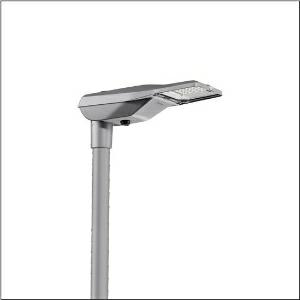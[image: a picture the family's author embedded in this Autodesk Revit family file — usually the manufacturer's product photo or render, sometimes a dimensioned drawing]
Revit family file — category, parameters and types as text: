
# Revit family: streetlight_sl_21_iq_micro___st1_0ab_5xe1m31u08db_013b
name_source: partatom
category: Lighting Fixtures
units: mm (PartAtom-declared; Revit-internal decimal feet)

## family parameters
Cut with Voids When Loaded = No
Host = Face
Light Source = No
Part Type = Normal
Room Calculation Point = No
Round Connector Dimension = Use Diameter
Shared = No

## types (1)
- --- (1 x LED, 4490 lm, 39.1 W, 3000K)
    Apparent Load = 39 VA
    CIE Flux Codes = 38 73 97 100 100
    Color Rendering = 70
    Color Temperature = 3000K
    Default Elevation = 1800 mm
    Description = Streetlight SL 21 iQ micro, mast luminaire, primary light control with lens, of PMMA, primary optical cover: cover, of toughened safety glass, transparent, light distribution: ST1.0aB, light emission: direct distribution, primary light characteristic: asymmetric, installation type: post-top, side-entry, LED, High Power LED, rated luminous flux: 4.490lm, luminous efficacy: 115lm/W, light colour: 730, colour temperature: 3000K, control gear: iQ-Street Remote, D4i with power reduction, control: pre-setting: logarithmic dimming characteristic, Street-Remote, Auto-Match, Temp-Guard, Lumen-Switch, Night-Set, Smart-Wire, Light-Fading, Desk-Remote (wireless, voltage-free reading and setting of iQ features in the workshop via application-optimized NFC function/RFID function), optimised constant luminous flux control (CLO 2.0), mains connection: 220..240V, AC, 50/60Hz, start of lifetime: 39W, end of service life: 41W, reduction: 17W, luminaire housing, of diecast aluminium, powder-coated, SITECO metallic grey (DB 702S), corrosivity category C5 high according to DIN EN ISO 12944, please order mast flange separately, inclination adjustable: 0°, 5°, 10°, 15°, sealing non-destructively replaceable, multi-level sealing system, length: 528mm, width: 235mm, height: 110mm, mast flange for spigot size: 42mm (side-entry): 5XC10008XM4, 60/48mm (side-entry/post-top): 5XC10108XM2, 76/60mm (side-entry/post-top): 5XC10108XM1, mounting height: 4..8m, Smart Interface below, protection rating (complete): IP66, insulation class (complete): insulation class II (safety insulation), certification: CE, ENEC, ENEC+, VDE, impact resistance: IK10, permissible operating ambient temperature for outdoor applications: -40..+50°C, standard-compliant lighting for roads and squares, packaging unit: 1 piece

Light Distribution: ST1.0aB
    Height = 110 mm
    Lamp = 1 x LED
    Lamp Light Flux = 4490 lm
    Lamp Power = 39.1 W
    Lamp count = 1
    Length = 528 mm
    Luminous efficacy = 115 lm/W
    Manufacturer = Siteco
    ModVariant = No
    Model = 5XE1M31U08DB
    Number of Poles = 1
    OnlyDefault = Yes
    Power Factor = 1
    Product Name = Streetlight SL 21 iQ micro | ST1.0aB
    Product group = mast luminaire | pylon top
    ProductGroupID = 6100
    Protection Class = Protection class II
    Protection Degree = IP 66
    RLX_Detail_Level = 1
    RLX_Emergency_Light_Flux = 0 lm
    RLX_Emergency_Type = 0
    RLX_Emergency_Type_DB = No
    RlxData = <blob elided: 98709 chars, md5=8e058868>
    Socket = socket
    Standby Power = 0 W
    System Light Flux = 4490 lm
    System Power = 39 W
    Type Comments = factory setting: luminous flux: 100 % | dim-lin: 254 | 765 mA
    Type Image = l_1277290.jpg
    URL = http://relux.com
    VarID = @adj_112777
    Voltage = 0 V
    Weight = 0.00 kg
    Width = 235 mm

## geometry (parser evidence)
native form markers: Blend x4, Sweep x10
no freeform markers — native parametric forms only
